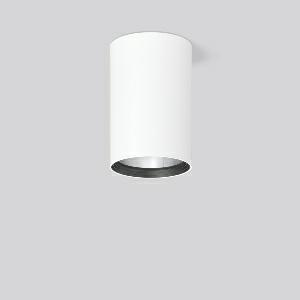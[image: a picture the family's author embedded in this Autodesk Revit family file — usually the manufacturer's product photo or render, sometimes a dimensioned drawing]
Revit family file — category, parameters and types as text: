
# Revit family: heledon_maxi_a_931224_002_76_e182
name_source: partatom
category: Lighting Fixtures
units: mm (PartAtom-declared; Revit-internal decimal feet)

## family parameters
Cut with Voids When Loaded = No
Host = Face
Light Source = No
Part Type = Normal
Room Calculation Point = No
Round Connector Dimension = Use Diameter
Shared = No

## types (1)
- HELEDON maxi A (1 x LED Modul 930, 4300 lm, 3000)
    Apparent Load = 35 VA
    Approval mark = CE
    CIE Flux Codes = 100 100 100 100 100
    Color Rendering = 90
    Color Temperature = 3000
    Default Elevation = 1800 mm
    Description = Series: HELEDON maxi
Cylindrical surface-mounted downlight. Housing: die-cast aluminium, powder-coated. Internal ceiling frame polycarbonate with bayonet mounting. Black plastic ring and recessed LED to prevent glare from the side. Optical assembly with reflector made of MIRO-Silver with 98% total light reflection for outstanding efficiency - can be changed without tools. Best colour rendering index Ra>90. Suitable for Ceiling mounting. Easy installation with a separate ceiling frame with bayonet mounting and plug connection. Driver integrated. Connected via plug-in connector. High quality converter without flickering and stroboscopic effect. The following accessories can be mounted without use of tools: interchangeable lenses, decorative glasses, honeycomb louvre, clear and frosted diffusers, white interchangeable plastic ring. 
Colour: traffic white, matt (RAL 9016)
Diameter: 123 mm
Height: 183 mm
Lamp: LED
Socket: without socket
Colour temperature: 3000K
Colour rendering index (CRI): 92
System power: 35 W
Rated luminous flux: 4300 lm
Luminous efficiency: 123 lm/W
Control gear: Converter, dimmable, DALI
Protection class: I
Type of protection: IP 20
    Height = 183 mm
    Lamp = 1 x LED Modul 930
    Lamp Light Flux = 4300 lm
    Lamp count = 1
    Length = 123 mm
    Lifetime = 50000 h
    Luminous efficacy = 123 lm/W
    Manufacturer = RZB
    ModVariant = No
    Model = 931224.002.76
    Mounting Place = Ceiling
    Mounting Type = Surface mounted
    Number of Poles = 1
    OnlyDefault = Yes
    Power Factor = 1
    Product Name = HELEDON maxi A
    Product group = Surface mounted downlights
    ProductGroupID = 302
    Protection Class = Protection class I
    Protection Degree = IP 20
    RLX_Detail_Level = 1
    RLX_Emergency_Light_Flux = 0 lm
    RLX_Emergency_Type = 0
    RLX_Emergency_Type_DB = No
    RlxData = <blob elided: 97477 chars, md5=1cd59597>
    Socket = socket
    Standby Power = 0 W
    System Light Flux = 4300 lm
    System Power = 35 W
    Type Comments = Product without accessories
    Type Image = 931192.002.jpg
    URL = http://relux.com
    VarID = ---
    Voltage = 230 V
    Voltage Range = 220-240 V
    Weight = 0.00 kg
    Width = 0 mm  [stored 0 ft]

note: [stored X ft] marks values corroborated as IEEE doubles in the binary element streams (Revit-internal decimal feet)

## geometry (parser evidence)
native form markers: Blend x4, Sweep x10
no freeform markers — native parametric forms only
